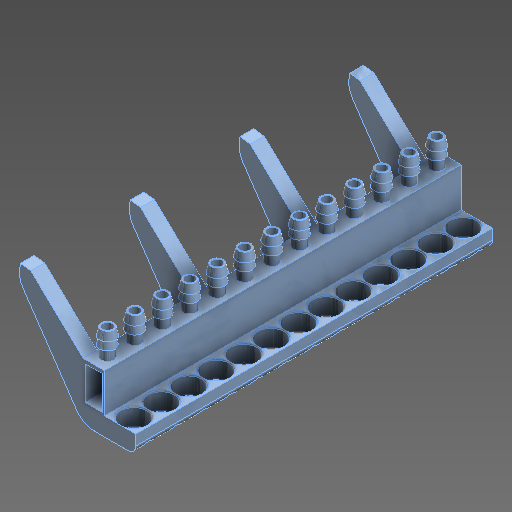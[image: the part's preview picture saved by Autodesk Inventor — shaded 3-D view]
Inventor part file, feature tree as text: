
AUTODESK INVENTOR PART (.ipt)
format: ipt  version: 2020 (Build 240168000, 168)  size: 679,424 bytes
history: native  units: in
note: dims shown in document units (in); Inventor stores cm internally (conversion verified against a paired STEP export)
features: other x11, extrude x7, pattern_linear x4, fillet x3, projected_geometry x1, sketch x1
ambient origin geometry x8: Origin, YZ Plane, XZ Plane, XY Plane, X Axis, Y Axis, Z Axis, Center Point
bodies: Body1 (feature_tree)
feature tree (27):
  other  "CrossSection1"
  other  "Silicone Fitting Plane"
  other  "Cap Plane"
  other  "Base Sketch"
  extrude  "Base"  Depth=0.3214in
  extrude  "Lip"  Depth=0.3214in
  extrude  "Tube Socket"  Depth=0.3214in
  pattern_linear  "Tube Socket Repetition"  Spacing1=0.0197in  [1 undecoded]
  other  "Silicone Fitting"
  pattern_linear  "Silicone Fitting Repetion"  Spacing1=0.5906in  [1 undecoded]
  extrude  "Airflow Cut"  [1 undecoded]
  pattern_linear  "Airflow Cut Repetition"  Spacing1=0.0in  [1 undecoded]
  extrude  "Coupling"  TaperAngle=90.0deg  [1 undecoded]
  extrude  "Cap"  Depth=0.3214in TaperAngle=0.0deg
  extrude  "Arm"  [1 undecoded]
  fillet  "Fillet4"  Radius=5.5118in
  fillet  "Fillet6"  Radius=0.4134in
  other  "Rule Fillet2"
  pattern_linear  "Rectangular Pattern9"  Count1=13  [1 undecoded]
  fillet  "Fillet5"  Radius=0.4134in
  other  "Silicone Fitting Sketch"
  other  "Airflow Cut Sketch"
  projected_geometry  "Projected Loop7"
  other  "Lip Sketch"
  sketch  "Sketch23"  dims[d87=0.0197in d88=0.0787in d89=-1.0625in d90=0.7874in d1=0.0591in d2=0.0591in d3=0.0591in d4=0.0197in d5=0.5906in d6=-0.2067in d8=0.0in d111=90.0deg d112=0.1181in d9=0.0in d12=-5.374in d155=5.5118in d157=0.4134in d158=5.1181in d160=0.4134in d161=5.374in d163=0.3214in d164=0.0in d165=0.4724in d166=0.0in d167=0.3937in d168=0.2067in d169=0.2362in d170=0.3937in d171=0.0in d172=5.1181in d174=0.4134in d188=0.0157in d189=0.3214in d190=0.5906in d200=0.2067in d201=0.0in d202=1.5748in d204=1.6535in d206=0.1181in d207=0.315in d209=0.315in d210=0.0295in d211=0.0295in d212=0.0295in d213=0.0591in d214=0.4134in d215=0.0in d218=0.5906in d219=0.3214in d220=0.0591in d221=0.0in d223=0.0481in]
  other  "Arm Sketch"
  other  "Cap Sketch"
note: 7 required parameter values undecoded (feature->parameter linkage not recoverable at this tier; creation-order binding heuristic only, values carry confidence <= 0.55)
